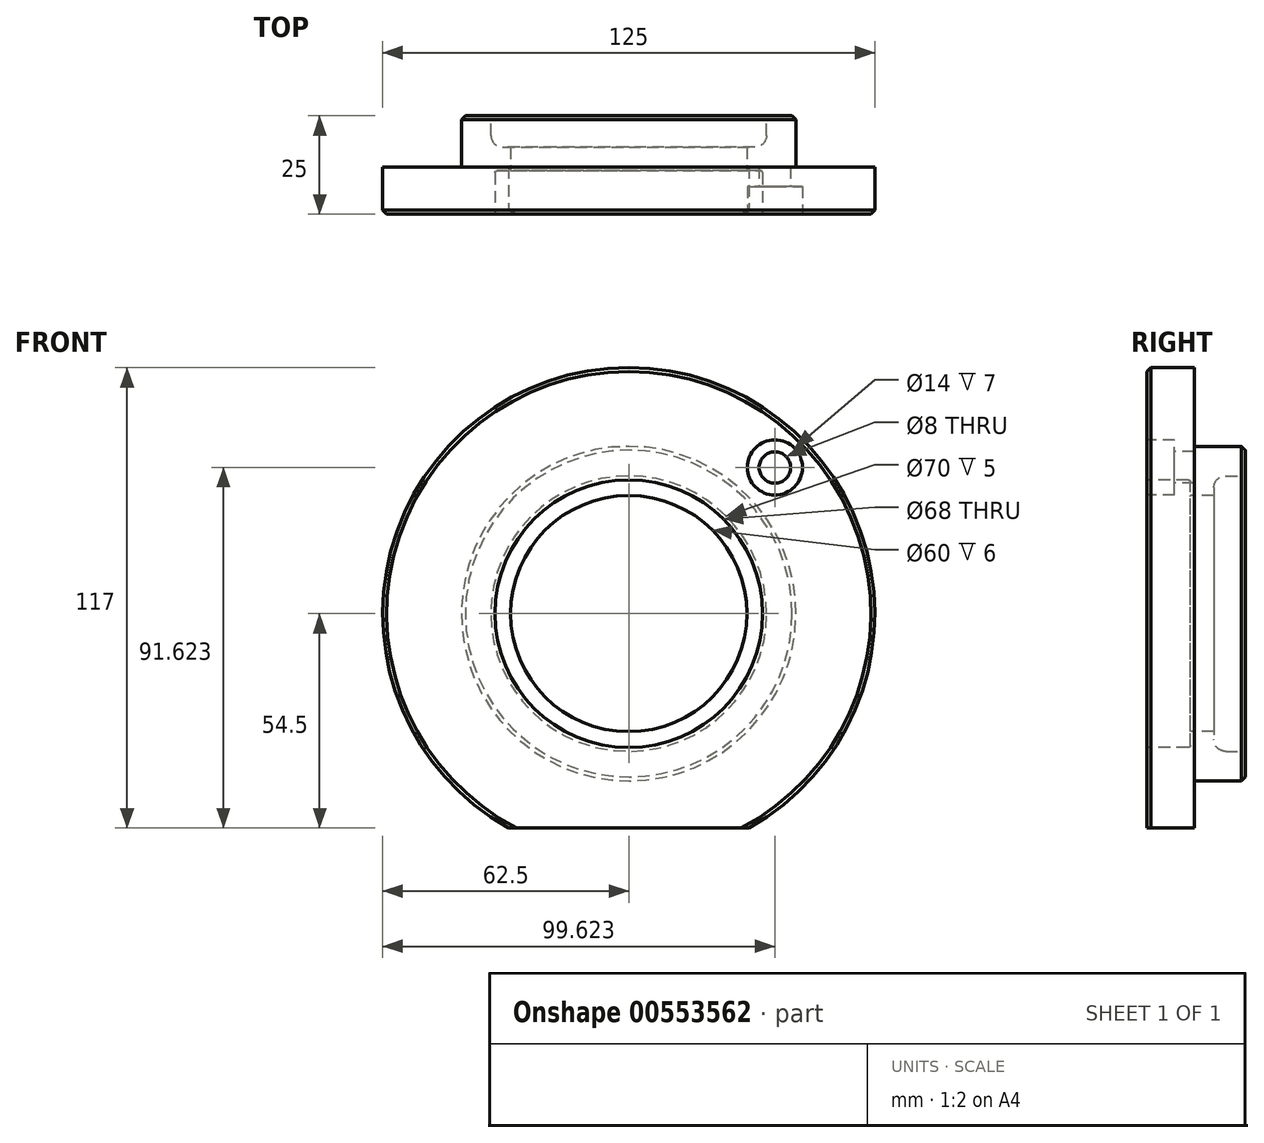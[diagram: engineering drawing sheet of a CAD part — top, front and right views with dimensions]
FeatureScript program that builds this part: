
annotation { "Feature Type Name" : "Feature", "Feature Type Description" : "" }
export const myFeature = defineFeature(function(context is Context, id is Id, definition is map)
    precondition{}
    {
        {
            var Q0;
            Q0=qCreatedBy(makeId("Front.planeOp"),FACE);
            var sketch = newSketch(context, id + "F0", { "sketchPlane" : qUnion([Q0])});
            skCircle(sketch, "E0", {"center": v(0, 0) * mm, "radius": 62.5 * mm});
            skSolve(sketch);
        }
        {
            var Q0;
            Q0=makeQuery(id+"F0.imprint","IMPRINT",FACE,{"disambiguationData":[TD([[makeQuery(id+"F0.imprint","IMPRINT",EDGE,{"derivedFrom":sQuery(id+"F0.wireOp",EDGE,"E0")}),1.0]])]});
            extrude(context, id + "F1", {"entities" : qUnion([Q0]), "oppositeDirection" : true, "depth" : 12 * mm, "offsetDistance" : 25 * mm});
        }
        {
            var Q0;
            Q0=makeQuery(id+"F1.opExtrude","CAP_FACE",FACE,{"disambiguationData":[OSD([sQuery(id+"F0.wireOp",EDGE,"E0")])],"isStart":true});
            var sketch = newSketch(context, id + "F2", { "sketchPlane" : qUnion([Q0])});
            skCircle(sketch, "E1", {"center": v(0, 0) * mm, "radius": 52.5 * mm, "construction": true});
            skLineSegment(sketch, "E2", {"start": v(0, 0) * mm, "end": v(37.12, 37.12) * mm, "construction": true});
            skCircle(sketch, "E3", {"center": v(37.12, 37.12) * mm, "radius": 7 * mm});
            skSolve(sketch);
        }
        {
            var Q0;
            Q0=makeQuery(id+"F2.imprint","IMPRINT",FACE,{"disambiguationData":[TD([[makeQuery(id+"F2.imprint","IMPRINT",EDGE,{"derivedFrom":sQuery(id+"F2.wireOp",EDGE,"E3")}),1.0]])]});
            extrude(context, id + "F3", {"entities" : qUnion([Q0]), "operationType" : NewBodyOperationType.REMOVE, "oppositeDirection" : true, "depth" : 7 * mm, "offsetDistance" : 25 * mm});
        }
        {
            var Q0;
            Q0=makeQuery(id+"F3.boolean.opBoolean","COPY",FACE,{"derivedFrom":makeQuery(id+"F3.opExtrude","CAP_FACE",FACE,{"disambiguationData":[OSD([sQuery(id+"F2.wireOp",EDGE,"E3")])],"isStart":false})});
            var sketch = newSketch(context, id + "F4", { "sketchPlane" : qUnion([Q0])});
            skCircle(sketch, "E4", {"center": v(37.12, 37.12) * mm, "radius": 4 * mm});
            skSolve(sketch);
        }
        {
            var Q0;
            Q0=makeQuery(id+"F4.imprint","IMPRINT",FACE,{"disambiguationData":[TD([[makeQuery(id+"F4.imprint","IMPRINT",EDGE,{"derivedFrom":sQuery(id+"F4.wireOp",EDGE,"E4")}),1.0]])]});
            extrude(context, id + "F5", {"entities" : qUnion([Q0]), "operationType" : NewBodyOperationType.REMOVE, "oppositeDirection" : true, "depth" : 25 * mm, "offsetDistance" : 25 * mm});
        }
        {
            var Q0;
            Q0=makeQuery(id+"F1.opExtrude","CAP_FACE",FACE,{"disambiguationData":[OSD([sQuery(id+"F0.wireOp",EDGE,"E0")])],"isStart":true});
            var sketch = newSketch(context, id + "F6", { "sketchPlane" : qUnion([Q0])});
            skLineSegment(sketch, "E5", {"start": v(0, 0) * mm, "end": v(0, -54.5) * mm, "construction": true});
            skLineSegment(sketch, "E6.bottom", {"start": v(-44.87, -68.42) * mm, "end": v(49.43, -68.42) * mm});
            skLineSegment(sketch, "E6.top", {"start": v(-44.87, -54.5) * mm, "end": v(49.43, -54.5) * mm});
            skLineSegment(sketch, "E6.left", {"start": v(-44.87, -68.42) * mm, "end": v(-44.87, -54.5) * mm});
            skLineSegment(sketch, "E6.right", {"start": v(49.43, -68.42) * mm, "end": v(49.43, -54.5) * mm});
            skSolve(sketch);
        }
        {
            var Q0;
            {var subQ0=sQuery(id+"F6.wireOp",EDGE,"E6.top");var subQ1=makeQuery(id+"F1.opExtrude","CAP_EDGE",EDGE,{"disambiguationData":[OSD([sQuery(id+"F0.wireOp",EDGE,"E0")])],"isStart":true});var subQ2=makeQuery(id+"F6.imprint","INTERSECT",VERTEX,{"disambiguationData":[OD(0.0)],"derivedFrom":[subQ1,subQ0]});Q0=makeQuery(id+"F6.imprint","IMPRINT",FACE,{"disambiguationData":[TD([[makeQuery(id+"F6.imprint","IMPRINT",EDGE,{"disambiguationData":[TD([[subQ2,-1.0]])],"derivedFrom":subQ0}),-1.0]])]});}
            extrude(context, id + "F7", {"entities" : qUnion([Q0]), "operationType" : NewBodyOperationType.REMOVE, "oppositeDirection" : true, "depth" : 25 * mm, "offsetDistance" : 25 * mm});
        }
        {
            var Q0;
            Q0=makeQuery(id+"F1.opExtrude","CAP_FACE",FACE,{"disambiguationData":[OSD([sQuery(id+"F0.wireOp",EDGE,"E0")])],"isStart":false});
            var sketch = newSketch(context, id + "F8", { "sketchPlane" : qUnion([Q0])});
            skCircle(sketch, "E7", {"center": v(0, 0) * mm, "radius": 42.5 * mm});
            skSolve(sketch);
        }
        {
            var Q0;
            Q0=makeQuery(id+"F8.imprint","IMPRINT",FACE,{"disambiguationData":[TD([[makeQuery(id+"F8.imprint","IMPRINT",EDGE,{"derivedFrom":sQuery(id+"F8.wireOp",EDGE,"E7")}),1.0]])]});
            extrude(context, id + "F9", {"entities" : qUnion([Q0]), "operationType" : NewBodyOperationType.ADD, "depth" : 13 * mm, "offsetDistance" : 25 * mm});
        }
        {
            var Q0;
            Q0=makeQuery(id+"F9.opExtrude","CAP_FACE",FACE,{"disambiguationData":[OSD([sQuery(id+"F8.wireOp",EDGE,"E7")])],"isStart":false});
            var sketch = newSketch(context, id + "F10", { "sketchPlane" : qUnion([Q0])});
            skCircle(sketch, "E8", {"center": v(0, 0) * mm, "radius": 35 * mm});
            skSolve(sketch);
        }
        {
            var Q0;
            Q0=makeQuery(id+"F10.imprint","IMPRINT",FACE,{"disambiguationData":[TD([[makeQuery(id+"F10.imprint","IMPRINT",EDGE,{"derivedFrom":sQuery(id+"F10.wireOp",EDGE,"E8")}),1.0]])]});
            extrude(context, id + "F11", {"entities" : qUnion([Q0]), "operationType" : NewBodyOperationType.REMOVE, "oppositeDirection" : true, "depth" : 8 * mm, "offsetDistance" : 25 * mm});
        }
        {
            var Q0;
            Q0=makeQuery(id+"F1.opExtrude","CAP_FACE",FACE,{"disambiguationData":[OSD([sQuery(id+"F0.wireOp",EDGE,"E0")])],"isStart":true});
            var sketch = newSketch(context, id + "F12", { "sketchPlane" : qUnion([Q0])});
            skCircle(sketch, "E9", {"center": v(0, 0) * mm, "radius": 34 * mm});
            skSolve(sketch);
        }
        {
            var Q0;
            Q0=makeQuery(id+"F12.imprint","IMPRINT",FACE,{"disambiguationData":[TD([[makeQuery(id+"F12.imprint","IMPRINT",EDGE,{"derivedFrom":sQuery(id+"F12.wireOp",EDGE,"E9")}),1.0]])]});
            extrude(context, id + "F13", {"entities" : qUnion([Q0]), "operationType" : NewBodyOperationType.REMOVE, "oppositeDirection" : true, "depth" : 11 * mm, "offsetDistance" : 25 * mm});
        }
        {
            var Q0;
            Q0=makeQuery(id+"F13.boolean.opBoolean","COPY",FACE,{"derivedFrom":makeQuery(id+"F13.opExtrude","CAP_FACE",FACE,{"disambiguationData":[OSD([sQuery(id+"F12.wireOp",EDGE,"E9")])],"isStart":false})});
            var sketch = newSketch(context, id + "F14", { "sketchPlane" : qUnion([Q0])});
            skCircle(sketch, "E10", {"center": v(0, 0) * mm, "radius": 30 * mm});
            skSolve(sketch);
        }
        {
            var Q0;
            Q0=makeQuery(id+"F14.imprint","IMPRINT",FACE,{"disambiguationData":[TD([[makeQuery(id+"F14.imprint","IMPRINT",EDGE,{"derivedFrom":sQuery(id+"F14.wireOp",EDGE,"E10")}),1.0]])]});
            extrude(context, id + "F15", {"entities" : qUnion([Q0]), "operationType" : NewBodyOperationType.REMOVE, "oppositeDirection" : true, "depth" : 25 * mm, "offsetDistance" : 25 * mm});
        }
        {
            var Q0;
            Q0=makeQuery(id+"F1.opExtrude","CAP_EDGE",EDGE,{"disambiguationData":[OSD([sQuery(id+"F0.wireOp",EDGE,"E0")])],"isStart":true});
            var Q1;
            Q1=makeQuery(id+"F13.boolean.opBoolean","COPY",EDGE,{"derivedFrom":makeQuery(id+"F13.opExtrude","CAP_EDGE",EDGE,{"disambiguationData":[OSD([sQuery(id+"F12.wireOp",EDGE,"E9")])],"isStart":true})});
            var Q2;
            Q2=makeQuery(id+"F9.opExtrude","CAP_EDGE",EDGE,{"disambiguationData":[OSD([sQuery(id+"F8.wireOp",EDGE,"E7")])],"isStart":false});
            chamfer(context, id + "F16", {"entities" : qUnion([Q0, Q1, Q2]), "width" : 1 * mm, "tangentPropagation" : true});
        }
        {
            var Q0;
            Q0=makeQuery(id+"F13.boolean.opBoolean","COPY",EDGE,{"derivedFrom":makeQuery(id+"F13.opExtrude","CAP_EDGE",EDGE,{"disambiguationData":[OSD([sQuery(id+"F12.wireOp",EDGE,"E9")])],"isStart":false})});
            var Q1;
            Q1=makeQuery(id+"F9.opExtrude","CAP_EDGE",EDGE,{"disambiguationData":[OSD([sQuery(id+"F8.wireOp",EDGE,"E7")])],"isStart":true});
            fillet(context, id + "F17", {"entities" : qUnion([Q0, Q1]), "radius" : .5 * mm, "tangentPropagation" : true, "allowEdgeOverflow" : false});
        }
        {
            var Q0;
            Q0=makeQuery(id+"F11.boolean.opBoolean","COPY",EDGE,{"derivedFrom":makeQuery(id+"F11.opExtrude","CAP_EDGE",EDGE,{"disambiguationData":[OSD([sQuery(id+"F10.wireOp",EDGE,"E8")])],"isStart":false})});
            fillet(context, id + "F18", {"entities" : qUnion([Q0]), "radius" : 3 * mm, "tangentPropagation" : true, "allowEdgeOverflow" : false});
        }
        {
            var Q0;
            Q0=qCreatedBy(makeId("Top.planeOp"),FACE);
            var sketch = newSketch(context, id + "F19", { "sketchPlane" : qUnion([Q0])});
            skLineSegment(sketch, "E11", {"start": v(23, 0) * mm, "end": v(34, 0) * mm});
            skLineSegment(sketch, "E12", {"start": v(34, 0) * mm, "end": v(34, 10.5) * mm});
            skLineSegment(sketch, "E13", {"start": v(33.5, 11) * mm, "end": v(30, 11) * mm});
            skLineSegment(sketch, "E14", {"start": v(30, 11) * mm, "end": v(30, 17) * mm});
            skLineSegment(sketch, "E15", {"start": v(30, 17) * mm, "end": v(23, 17) * mm});
            skLineSegment(sketch, "E16", {"start": v(23, 17) * mm, "end": v(23, 0) * mm});
            skPoint(sketch, "E17.visualSharp", {"position": v(34, 11) * mm});
            skArc(sketch, "E17.filletArc", {"start": v(34, 10.5) * mm, "mid": v(33.85, 10.85) * mm, "end": v(33.5, 11) * mm});
            skSolve(sketch);
        }
        {
            var Q0;
            Q0 = qSketchRegion(id + "F19", true);
            var Q1;
            Q1=makeQuery(id+"F1.opExtrude","SWEPT_FACE",FACE,{"disambiguationData":[OSD([sQuery(id+"F0.wireOp",EDGE,"E0")])]});
            revolve(context, id + "F20", {"entities" : qUnion([Q0]), "axis" : qUnion([Q1]), "revolveType" : RevolveType.FULL});
        }
        {
            var Q0;
            Q0=makeQuery(id+"F20.opRevolve","SWEPT_BODY",BODY,{"disambiguationData":[OSD([sQuery(id+"F19.wireOp",EDGE,"E11"),sQuery(id+"F19.wireOp",EDGE,"E12"),sQuery(id+"F19.wireOp",EDGE,"E13"),sQuery(id+"F19.wireOp",EDGE,"E14"),sQuery(id+"F19.wireOp",EDGE,"E15"),sQuery(id+"F19.wireOp",EDGE,"E16"),sQuery(id+"F19.wireOp",EDGE,"E17.filletArc")])]});
            deleteBodies(context, id + "F21", {"entities" : qUnion([Q0])});
        }
    });
